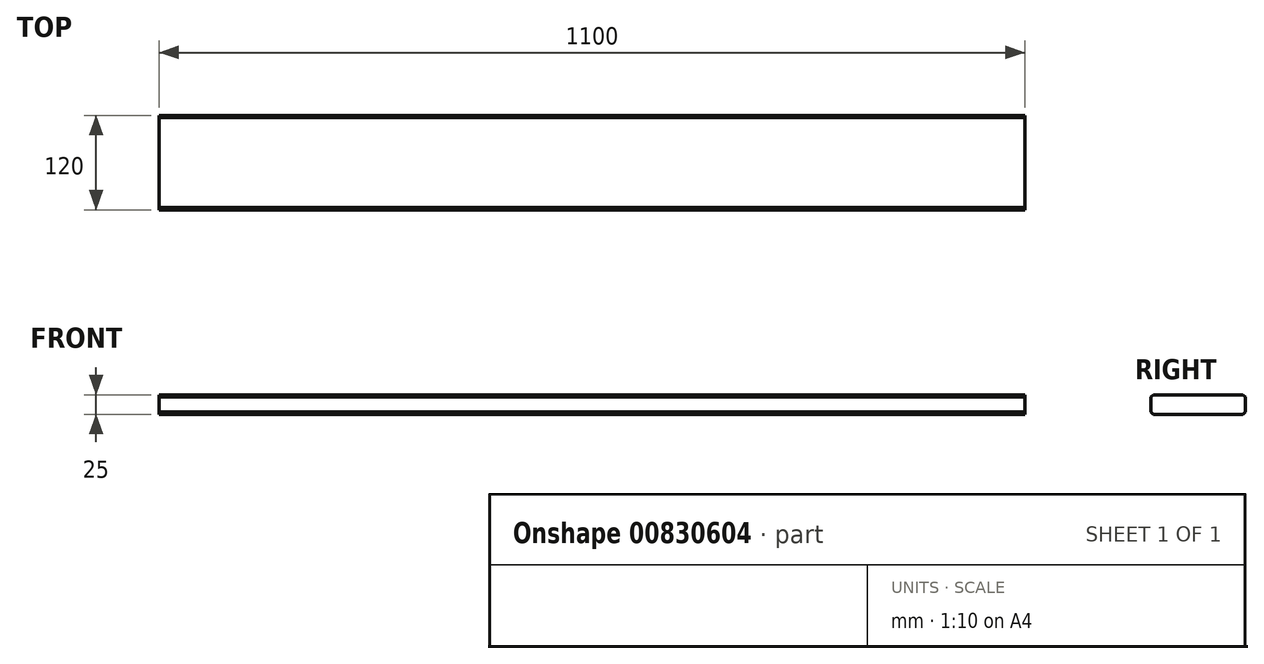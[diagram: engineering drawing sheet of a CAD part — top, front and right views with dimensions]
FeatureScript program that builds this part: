
annotation { "Feature Type Name" : "Feature", "Feature Type Description" : "" }
export const myFeature = defineFeature(function(context is Context, id is Id, definition is map)
    precondition{}
    {
        {
            var Q0;
            Q0=qCreatedBy(makeId("Right.planeOp"),FACE);
            var sketch = newSketch(context, id + "F0", { "sketchPlane" : qUnion([Q0])});
            skLineSegment(sketch, "E0.bottom", {"start": v(0, 0) * mm, "end": v(-120, 0) * mm});
            skLineSegment(sketch, "E0.top", {"start": v(0, 25) * mm, "end": v(-120, 25) * mm});
            skLineSegment(sketch, "E0.left", {"start": v(0, 0) * mm, "end": v(0, 25) * mm});
            skLineSegment(sketch, "E0.right", {"start": v(-120, 0) * mm, "end": v(-120, 25) * mm});
            skSolve(sketch);
        }
        {
            var Q0;
            Q0=makeQuery(id+"F0.imprint","IMPRINT",FACE,{"disambiguationData":[TD([[makeQuery(id+"F0.imprint","IMPRINT",EDGE,{"derivedFrom":sQuery(id+"F0.wireOp",EDGE,"E0.bottom")}),-1.0]])]});
            extrude(context, id + "F1", {"entities" : qUnion([Q0]), "depth" : 1100 * mm, "offsetDistance" : 25 * mm});
        }
        {
            var Q0;
            Q0=makeQuery(id+"F1.opExtrude","SWEPT_EDGE",EDGE,{"disambiguationData":[OSD([sQuery(id+"F0.wireOp",EDGE,"E0.top"),sQuery(id+"F0.wireOp",EDGE,"E0.left")])]});
            var Q1;
            Q1=makeQuery(id+"F1.opExtrude","SWEPT_EDGE",EDGE,{"disambiguationData":[OSD([sQuery(id+"F0.wireOp",EDGE,"E0.top"),sQuery(id+"F0.wireOp",EDGE,"E0.right")])]});
            var Q2;
            Q2=makeQuery(id+"F1.opExtrude","SWEPT_EDGE",EDGE,{"disambiguationData":[OSD([sQuery(id+"F0.wireOp",EDGE,"E0.bottom"),sQuery(id+"F0.wireOp",EDGE,"E0.right")])]});
            var Q3;
            Q3=makeQuery(id+"F1.opExtrude","SWEPT_EDGE",EDGE,{"disambiguationData":[OSD([sQuery(id+"F0.wireOp",EDGE,"E0.bottom"),sQuery(id+"F0.wireOp",EDGE,"E0.left")])]});
            chamfer(context, id + "F2", {"entities" : qUnion([Q0, Q1, Q2, Q3]), "width" : 3 * mm, "tangentPropagation" : true});
        }
    });
